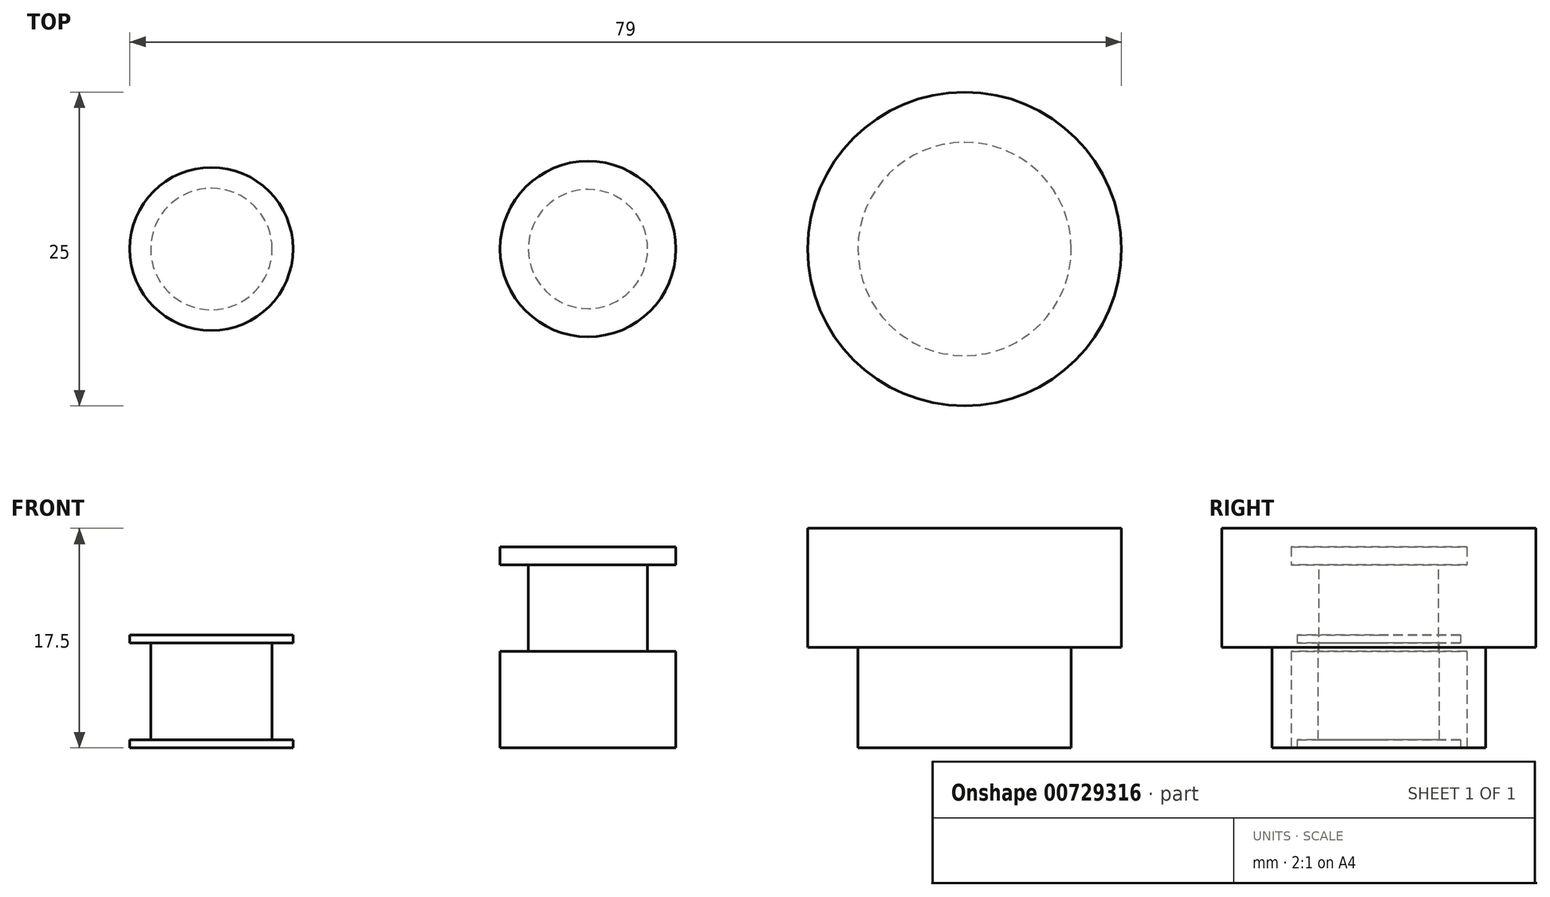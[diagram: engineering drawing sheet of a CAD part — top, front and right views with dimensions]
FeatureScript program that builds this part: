
annotation { "Feature Type Name" : "Feature", "Feature Type Description" : "" }
export const myFeature = defineFeature(function(context is Context, id is Id, definition is map)
    precondition{}
    {
        {
            var Q0;
            Q0=qCreatedBy(makeId("Top.planeOp"),FACE);
            var sketch = newSketch(context, id + "F0", { "sketchPlane" : qUnion([Q0])});
            skCircle(sketch, "E0", {"center": v(0, 0) * mm, "radius": 7 * mm});
            skSolve(sketch);
        }
        {
            var Q0;
            Q0 = qSketchRegion(id + "F0", true);
            var Q1;
            Q1=makeQuery(id+"F0.imprint","IMPRINT",FACE,{"disambiguationData":[TD([[makeQuery(id+"F0.imprint","IMPRINT",EDGE,{"derivedFrom":sQuery(id+"F0.wireOp",EDGE,"E0")}),1.0]])]});
            extrude(context, id + "F1", {"entities" : qUnion([Q0, Q1]), "depth" : 16 * mm, "offsetDistance" : 25 * mm});
        }
        {
            var Q0;
            Q0=qCreatedBy(makeId("Front.planeOp"),FACE);
            var sketch = newSketch(context, id + "F2", { "sketchPlane" : qUnion([Q0])});
            skLineSegment(sketch, "E1.bottom", {"start": v(7, 14.6) * mm, "end": v(4.75, 14.6) * mm});
            skLineSegment(sketch, "E1.top", {"start": v(7, 7.7) * mm, "end": v(4.75, 7.7) * mm});
            skLineSegment(sketch, "E1.left", {"start": v(7, 14.6) * mm, "end": v(7, 7.7) * mm});
            skLineSegment(sketch, "E1.right", {"start": v(4.75, 14.6) * mm, "end": v(4.75, 7.7) * mm});
            skLineSegment(sketch, "E2", {"start": v(0, 0) * mm, "end": v(0, 16.34) * mm, "construction": true});
            skSolve(sketch);
        }
        {
            var Q0;
            Q0=makeQuery(id+"F2.imprint","IMPRINT",FACE,{"disambiguationData":[TD([[makeQuery(id+"F2.imprint","IMPRINT",EDGE,{"derivedFrom":sQuery(id+"F2.wireOp",EDGE,"E1.bottom")}),1.0]])]});
            var Q1;
            Q1=sQuery(id+"F2.wireOp",EDGE,"E2");
            var Q2;
            Q2=sQuery(id+"F2.wireOp",EDGE,"E1.left");
            var Q3;
            Q3=sQuery(id+"F2.wireOp",EDGE,"E1.right");
            var Q4;
            Q4=sQuery(id+"F2.wireOp",EDGE,"E1.top");
            var Q5;
            Q5=sQuery(id+"F2.wireOp",EDGE,"E1.bottom");
            var Q6;
            Q6=sQuery(id+"F2.wireOp",EDGE,"E2");
            revolve(context, id + "F3", {"operationType" : NewBodyOperationType.REMOVE, "surfaceOperationType" : NewSurfaceOperationType.NEW, "entities" : qUnion([Q0]), "surfaceEntities" : qUnion([Q1, Q2, Q3, Q4, Q5]), "axis" : qUnion([Q6]), "revolveType" : RevolveType.FULL, "oppositeDirection" : true});
        }
        {
            var Q0;
            Q0=qCreatedBy(makeId("Top.planeOp"),FACE);
            var sketch = newSketch(context, id + "F4", { "sketchPlane" : qUnion([Q0])});
            skCircle(sketch, "E3", {"center": v(30, 0) * mm, "radius": 8.5 * mm});
            skSolve(sketch);
        }
        {
            var Q0;
            Q0=makeQuery(id+"F4.imprint","IMPRINT",FACE,{"disambiguationData":[TD([[makeQuery(id+"F4.imprint","IMPRINT",EDGE,{"derivedFrom":sQuery(id+"F4.wireOp",EDGE,"E3")}),1.0]])]});
            extrude(context, id + "F5", {"entities" : qUnion([Q0]), "depth" : 8 * mm, "offsetDistance" : 25 * mm});
        }
        {
            var Q0;
            Q0=makeQuery(id+"F5.opExtrude","CAP_FACE",FACE,{"disambiguationData":[OSD([sQuery(id+"F4.wireOp",EDGE,"E3")])],"isStart":false});
            var sketch = newSketch(context, id + "F6", { "sketchPlane" : qUnion([Q0])});
            skCircle(sketch, "E4", {"center": v(30, 0) * mm, "radius": 12.5 * mm});
            skSolve(sketch);
        }
        {
            var Q0;
            Q0=makeQuery(id+"F6.imprint","IMPRINT",FACE,{"disambiguationData":[TD([[makeQuery(id+"F6.imprint","IMPRINT",EDGE,{"derivedFrom":sQuery(id+"F6.wireOp",EDGE,"E4")}),1.0]])]});
            var Q1;
            Q1=makeQuery(id+"F6.imprint","IMPRINT",FACE,{"disambiguationData":[TD([[makeQuery(id+"F6.imprint","IMPRINT",EDGE,{"derivedFrom":makeQuery(id+"F5.opExtrude","CAP_EDGE",EDGE,{"disambiguationData":[OSD([sQuery(id+"F4.wireOp",EDGE,"E3")])],"isStart":false})}),1.0]])]});
            extrude(context, id + "F7", {"entities" : qUnion([Q0, Q1]), "operationType" : NewBodyOperationType.ADD, "depth" : 9.5 * mm, "offsetDistance" : 25 * mm});
        }
        {
            var Q0;
            Q0=qCreatedBy(makeId("Top.planeOp"),FACE);
            var sketch = newSketch(context, id + "F8", { "sketchPlane" : qUnion([Q0])});
            skPoint(sketch, "E5", {"position": v(-30, 0) * mm});
            skCircle(sketch, "E6", {"center": v(-30, 0) * mm, "radius": 6.5 * mm});
            skSolve(sketch);
        }
        {
            var Q0;
            Q0=makeQuery(id+"F8.imprint","IMPRINT",FACE,{"disambiguationData":[TD([[makeQuery(id+"F8.imprint","IMPRINT",EDGE,{"derivedFrom":sQuery(id+"F8.wireOp",EDGE,"E6")}),1.0]])]});
            extrude(context, id + "F9", {"entities" : qUnion([Q0]), "depth" : 9 * mm, "offsetDistance" : 25 * mm});
        }
        {
            var Q0;
            Q0=qCreatedBy(makeId("Front.planeOp"),FACE);
            var sketch = newSketch(context, id + "F10", { "sketchPlane" : qUnion([Q0])});
            skLineSegment(sketch, "E7", {"start": v(-30, 0) * mm, "end": v(-30, 7.63) * mm, "construction": true});
            skLineSegment(sketch, "E8.bottom", {"start": v(-34.84, 8.35) * mm, "end": v(-36.5, 8.35) * mm});
            skLineSegment(sketch, "E8.top", {"start": v(-34.84, 0.65) * mm, "end": v(-36.5, 0.65) * mm});
            skLineSegment(sketch, "E8.left", {"start": v(-34.84, 8.35) * mm, "end": v(-34.84, 0.65) * mm});
            skLineSegment(sketch, "E8.right", {"start": v(-36.5, 8.35) * mm, "end": v(-36.5, 0.65) * mm});
            skSolve(sketch);
        }
        {
            var Q0;
            Q0=makeQuery(id+"F10.imprint","IMPRINT",FACE,{"disambiguationData":[TD([[makeQuery(id+"F10.imprint","IMPRINT",EDGE,{"derivedFrom":sQuery(id+"F10.wireOp",EDGE,"E8.bottom")}),1.0]])]});
            var Q1;
            Q1=sQuery(id+"F10.wireOp",EDGE,"E7");
            revolve(context, id + "F11", {"operationType" : NewBodyOperationType.REMOVE, "surfaceOperationType" : NewSurfaceOperationType.NEW, "entities" : qUnion([Q0]), "axis" : qUnion([Q1]), "revolveType" : RevolveType.FULL, "oppositeDirection" : true});
        }
    });
